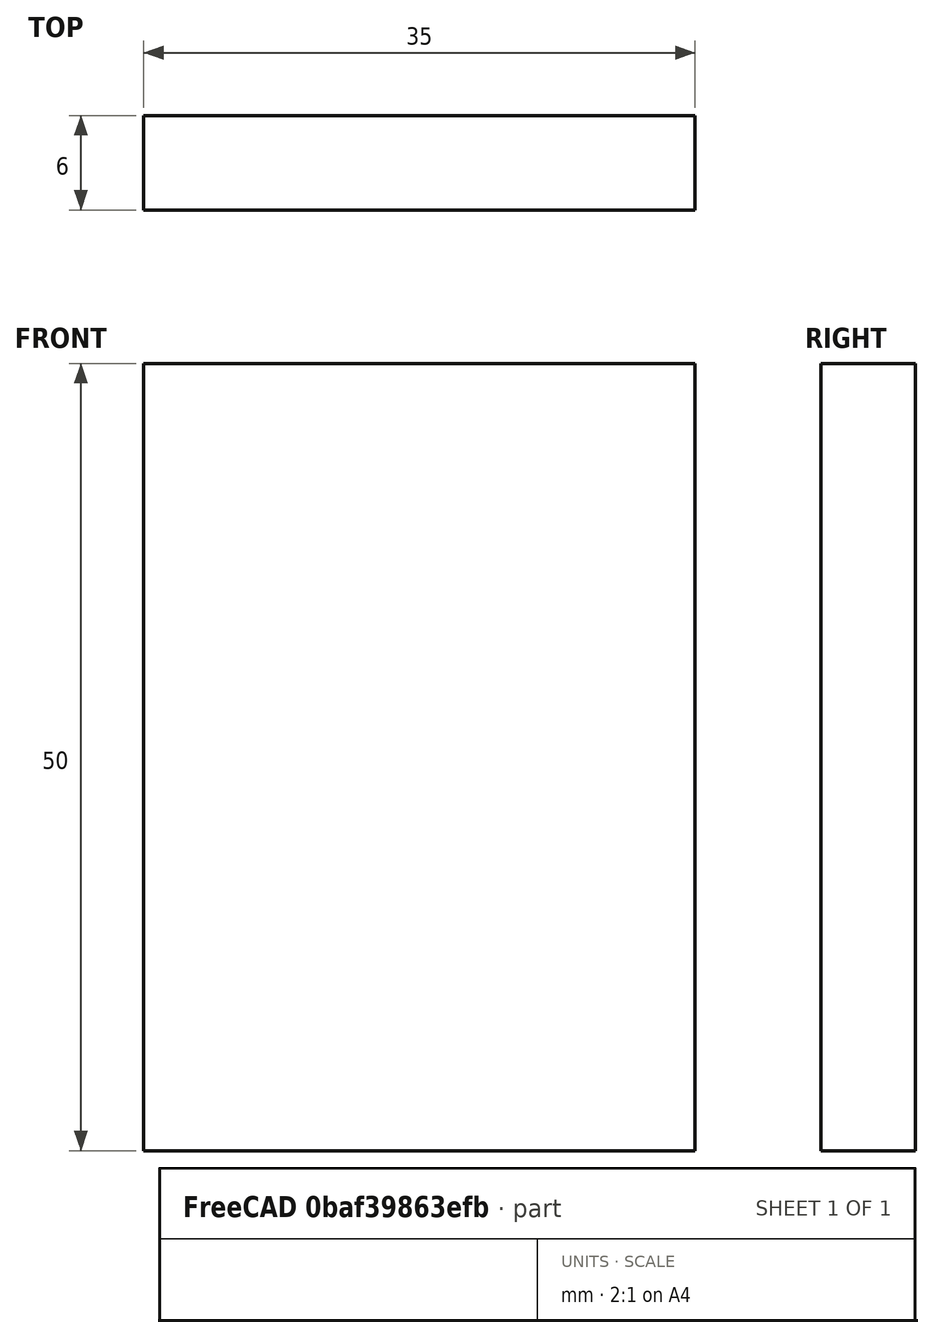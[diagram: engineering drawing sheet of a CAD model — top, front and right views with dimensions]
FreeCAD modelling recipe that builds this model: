
FCSTD DOCUMENT  (FreeCAD 0.15R4671 (Git))
Label: Flat Bar 35x6 EN10058 S235JR
License: All rights reserved
LicenseURL: http://en.wikipedia.org/wiki/All_rights_reserved
objects: Sketcher::SketchObject×1, Part::Extrusion×1
note: 2 computed .brp shape members not serialized (recipe doc carries the construction recipe); baked Part::Feature solids carry a one-line shape summary decoded from their .brp

FEATURE [Sketcher::SketchObject] Sketch
  sketch-geometry (4):
    g0: LineSegment StartX=-17.5 StartY=-3 StartZ=0 EndX=17.5 EndY=-3 EndZ=0
    g1: LineSegment StartX=17.5 StartY=-3 StartZ=0 EndX=17.5 EndY=3 EndZ=0
    g2: LineSegment StartX=17.5 StartY=3 StartZ=0 EndX=-17.5 EndY=3 EndZ=0
    g3: LineSegment StartX=-17.5 StartY=3 StartZ=0 EndX=-17.5 EndY=-3 EndZ=0
  constraints (12):
    c: Coincident(g0,g1)
    c: Coincident(g1,g2)
    c: Coincident(g2,g3)
    c: Coincident(g3,g0)
    c: Horizontal(g0)
    c: Horizontal(g2)
    c: Vertical(g1)
    c: Vertical(g3)
    c: Symmetric(g1,g2,g-2)
    c: Symmetric(g0,g1,g-1)
    c: DistanceY(g1) = 6
    c: DistanceX(g0) = 35
FEATURE [Part::Extrusion] Extrude  label="Flat Bar 35x6 EN10058 S235JR"
  Base = -> Sketch
  Dir = (0,0,50)
  Solid = true
